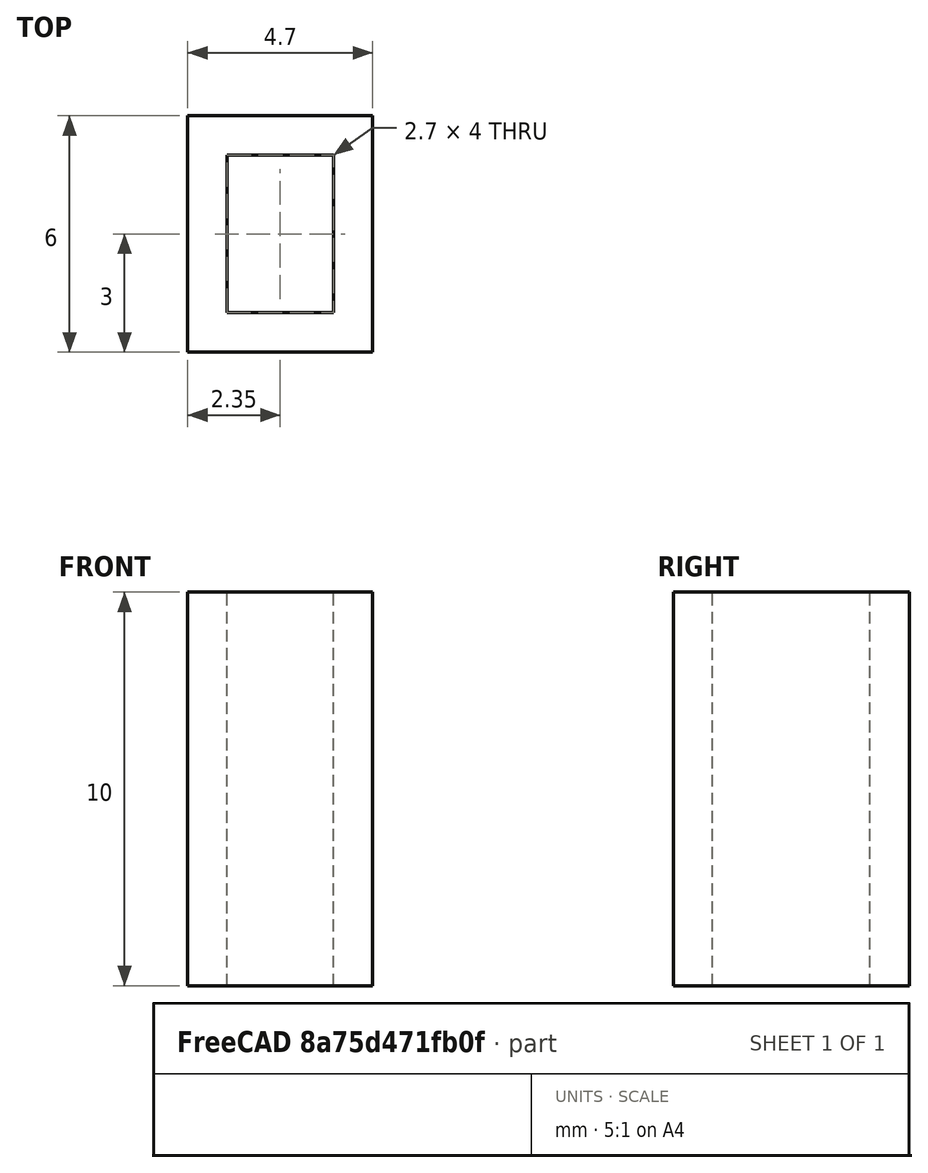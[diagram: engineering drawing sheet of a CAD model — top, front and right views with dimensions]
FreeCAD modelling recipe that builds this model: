
FCSTD DOCUMENT  (FreeCAD 0.16R6707 (Git))
Label: PhototransistorCover
License: All rights reserved
LicenseURL: http://en.wikipedia.org/wiki/All_rights_reserved
objects: Sketcher::SketchObject×1, PartDesign::Pad×1
note: 3 computed .brp shape members not serialized (recipe doc carries the construction recipe); baked Part::Feature solids carry a one-line shape summary decoded from their .brp

FEATURE [Sketcher::SketchObject] Sketch
  sketch-geometry (8):
    g0: LineSegment StartX=0 StartY=0 StartZ=0 EndX=2.7 EndY=0 EndZ=0
    g1: LineSegment StartX=2.7 StartY=0 StartZ=0 EndX=2.7 EndY=4 EndZ=0
    g2: LineSegment StartX=2.7 StartY=4 StartZ=0 EndX=0 EndY=4 EndZ=0
    g3: LineSegment StartX=0 StartY=4 StartZ=0 EndX=0 EndY=0 EndZ=0
    g4: LineSegment StartX=-1 StartY=-1 StartZ=0 EndX=3.7 EndY=-1 EndZ=0
    g5: LineSegment StartX=3.7 StartY=-1 StartZ=0 EndX=3.7 EndY=5 EndZ=0
    g6: LineSegment StartX=3.7 StartY=5 StartZ=0 EndX=-1 EndY=5 EndZ=0
    g7: LineSegment StartX=-1 StartY=5 StartZ=0 EndX=-1 EndY=-1 EndZ=0
  constraints (23):
    c: Coincident(g0,g1)
    c: Coincident(g1,g2)
    c: Coincident(g2,g3)
    c: Coincident(g3,g0)
    c: Horizontal(g0)
    c: Horizontal(g2)
    c: Vertical(g1)
    c: Vertical(g3)
    c: Distance(g0) = 2.7
    c: Distance(g3) = 4
    c: Coincident(g0,g-1)
    c: Coincident(g4,g5)
    c: Coincident(g5,g6)
    c: Coincident(g6,g7)
    c: Coincident(g7,g4)
    c: Horizontal(g4)
    c: Horizontal(g6)
    c: Vertical(g5)
    c: Vertical(g7)
    c: DistanceX(g4) = -1
    c: DistanceY(g4) = -1
    c: Distance(g4) = 4.7
    c: Distance(g5) = 6
FEATURE [PartDesign::Pad] Pad
  Length = 10
  Length2 = 100
  Sketch = -> Sketch
  Type = 0
